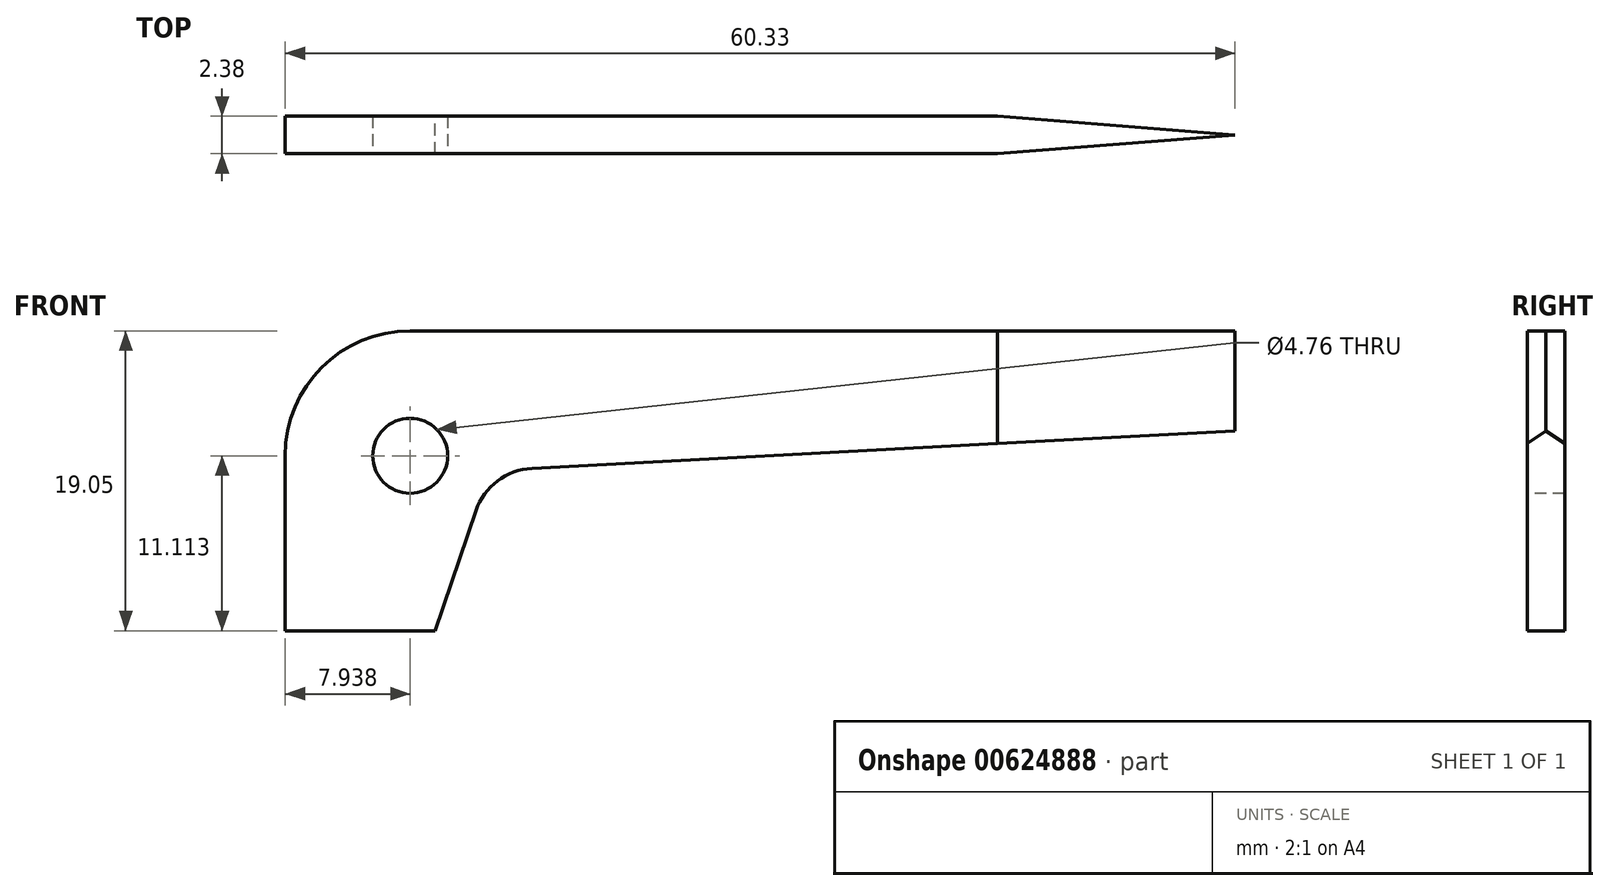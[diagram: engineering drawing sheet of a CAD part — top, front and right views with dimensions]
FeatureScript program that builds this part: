
annotation { "Feature Type Name" : "Feature", "Feature Type Description" : "" }
export const myFeature = defineFeature(function(context is Context, id is Id, definition is map)
    precondition{}
    {
        {
            var Q0;
            Q0=qCreatedBy(makeId("Front.planeOp"),FACE);
            var sketch = newSketch(context, id + "F0", { "sketchPlane" : qUnion([Q0])});
            skLineSegment(sketch, "E0.top", {"start": v(7.94, 19.05) * mm, "end": v(60.33, 19.05) * mm});
            skLineSegment(sketch, "E0.left", {"start": v(0, 0) * mm, "end": v(0, 11.11) * mm});
            skLineSegment(sketch, "E1", {"start": v(9.53, 0) * mm, "end": v(12.12, 7.63) * mm});
            skLineSegment(sketch, "E2", {"start": v(60.33, 12.7) * mm, "end": v(15.66, 10.31) * mm});
            skLineSegment(sketch, "E3", {"start": v(0, 0) * mm, "end": v(9.53, 0) * mm});
            skLineSegment(sketch, "E4", {"start": v(60.33, 12.7) * mm, "end": v(60.32, 19.05) * mm});
            skArc(sketch, "E5", {"start": v(15.66, 10.31) * mm, "mid": v(13.48, 9.51) * mm, "end": v(12.12, 7.63) * mm});
            skPoint(sketch, "E6.visualSharp", {"position": v(0, 19.05) * mm});
            skArc(sketch, "E6.filletArc", {"start": v(7.94, 19.05) * mm, "mid": v(2.32, 16.73) * mm, "end": v(0, 11.11) * mm});
            skSolve(sketch);
        }
        {
            var Q0;
            Q0 = qSketchRegion(id + "F0", true);
            extrude(context, id + "F1", {"entities" : qUnion([Q0]), "depth" : 2.38 * mm, "offsetDistance" : 25.4 * mm});
        }
        {
            var Q0;
            Q0=makeQuery(id+"F1.opExtrude","CAP_FACE",FACE,{"disambiguationData":[OSD([sQuery(id+"F0.wireOp",EDGE,"E0.top"),sQuery(id+"F0.wireOp",EDGE,"E0.left"),sQuery(id+"F0.wireOp",EDGE,"E1"),sQuery(id+"F0.wireOp",EDGE,"E2"),sQuery(id+"F0.wireOp",EDGE,"E3"),sQuery(id+"F0.wireOp",EDGE,"E4"),sQuery(id+"F0.wireOp",EDGE,"E5"),sQuery(id+"F0.wireOp",EDGE,"E6.filletArc")])],"isStart":false});
            var sketch = newSketch(context, id + "F2", { "sketchPlane" : qUnion([Q0])});
            skCircle(sketch, "E7", {"center": v(7.94, 11.11) * mm, "radius": 2.38 * mm});
            skSolve(sketch);
        }
        {
            var Q0;
            Q0=makeQuery(id+"F2.imprint","IMPRINT",FACE,{"disambiguationData":[TD([[makeQuery(id+"F2.imprint","IMPRINT",EDGE,{"derivedFrom":sQuery(id+"F2.wireOp",EDGE,"E7")}),1.0]])]});
            extrude(context, id + "F3", {"entities" : qUnion([Q0]), "operationType" : NewBodyOperationType.REMOVE, "oppositeDirection" : true, "depth" : 25.4 * mm, "offsetDistance" : 25.4 * mm});
        }
        {
            var Q0;
            Q0=makeQuery(id+"F1.opExtrude","SWEPT_FACE",FACE,{"disambiguationData":[OSD([sQuery(id+"F0.wireOp",EDGE,"E0.top")])]});
            var sketch = newSketch(context, id + "F4", { "sketchPlane" : qUnion([Q0])});
            skLineSegment(sketch, "E8", {"start": v(45.24, 0) * mm, "end": v(60.33, -1.2) * mm});
            skLineSegment(sketch, "E9", {"start": v(60.33, -1.2) * mm, "end": v(60.33, 0) * mm});
            skLineSegment(sketch, "E10", {"start": v(60.33, 0) * mm, "end": v(45.24, 0) * mm});
            skLineSegment(sketch, "E11.MirrorCS", {"start": v(45.24, -2.38) * mm, "end": v(60.33, -1.2) * mm});
            skLineSegment(sketch, "E12.MirrorCS", {"start": v(60.33, -2.38) * mm, "end": v(45.24, -2.38) * mm});
            skLineSegment(sketch, "E13.MirrorCS", {"start": v(60.33, -1.2) * mm, "end": v(60.33, -2.38) * mm});
            skSolve(sketch);
        }
        {
            var Q0;
            Q0=makeQuery(id+"F4.imprint","IMPRINT",FACE,{"disambiguationData":[TD([[makeQuery(id+"F4.imprint","IMPRINT",EDGE,{"derivedFrom":sQuery(id+"F4.wireOp",EDGE,"E11.MirrorCS")}),-1.0]])]});
            var Q1;
            Q1=makeQuery(id+"F4.imprint","IMPRINT",FACE,{"disambiguationData":[TD([[makeQuery(id+"F4.imprint","IMPRINT",EDGE,{"derivedFrom":sQuery(id+"F4.wireOp",EDGE,"E8")}),1.0]])]});
            extrude(context, id + "F5", {"entities" : qUnion([Q0, Q1]), "operationType" : NewBodyOperationType.REMOVE, "oppositeDirection" : true, "depth" : 25.4 * mm, "offsetDistance" : 25.4 * mm});
        }
    });
